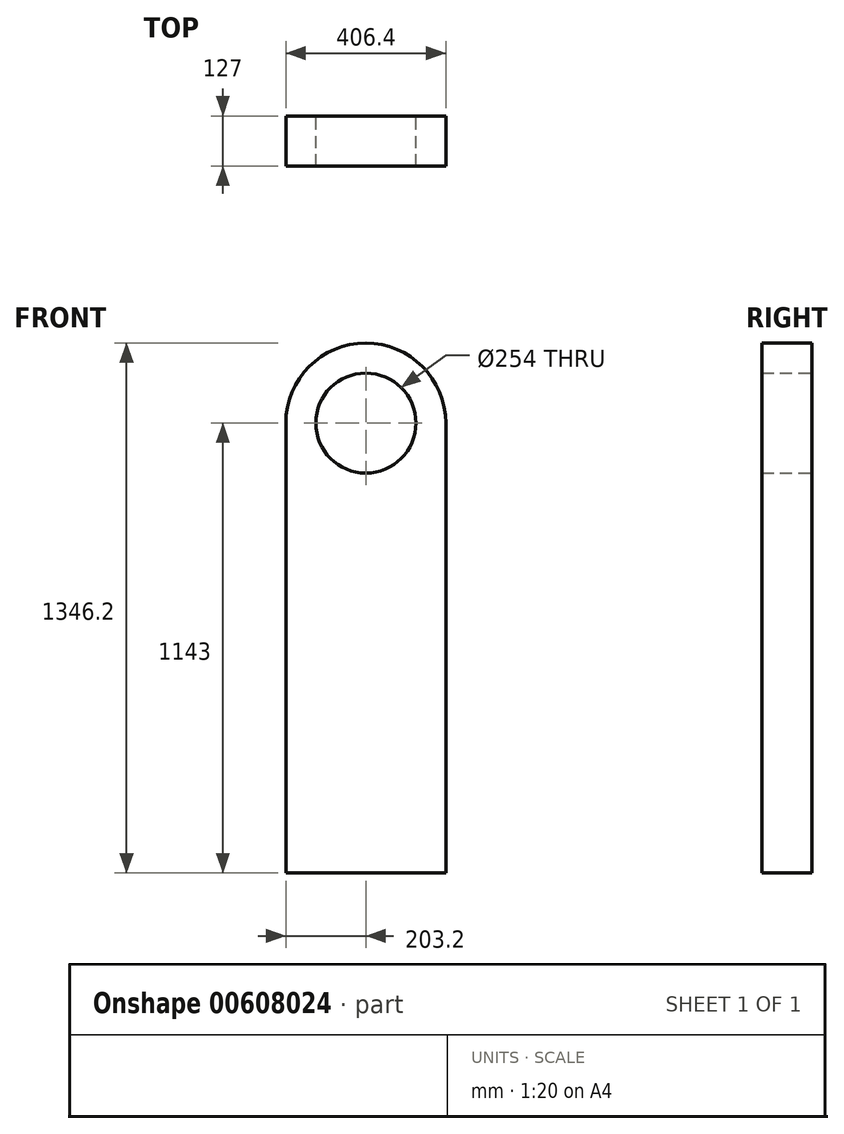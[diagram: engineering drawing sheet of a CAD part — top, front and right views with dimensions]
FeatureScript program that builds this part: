
annotation { "Feature Type Name" : "Feature", "Feature Type Description" : "" }
export const myFeature = defineFeature(function(context is Context, id is Id, definition is map)
    precondition{}
    {
        {
            var Q0;
            Q0=qCreatedBy(makeId("Front.planeOp"),FACE);
            var sketch = newSketch(context, id + "F0", { "sketchPlane" : qUnion([Q0])});
            skLineSegment(sketch, "E0.top", {"start": v(-203.2, -1143) * mm, "end": v(203.2, -1143) * mm});
            skLineSegment(sketch, "E0.left", {"start": v(-203.2, 0) * mm, "end": v(-203.2, -1143) * mm});
            skLineSegment(sketch, "E0.right", {"start": v(203.2, 0) * mm, "end": v(203.2, -1143) * mm});
            skArc(sketch, "E1", {"start": v(203.2, 0) * mm, "mid": v(0, 203.2) * mm, "end": v(-203.2, 0) * mm});
            skCircle(sketch, "E2", {"center": v(0, 0) * mm, "radius": 127 * mm});
            skSolve(sketch);
        }
        {
            var Q0;
            Q0 = qSketchRegion(id + "F0", true);
            extrude(context, id + "F1", {"entities" : qUnion([Q0]), "endBound" : BoundingType.SYMMETRIC, "depth" : 127 * mm, "offsetDistance" : 25.4 * mm});
        }
    });
